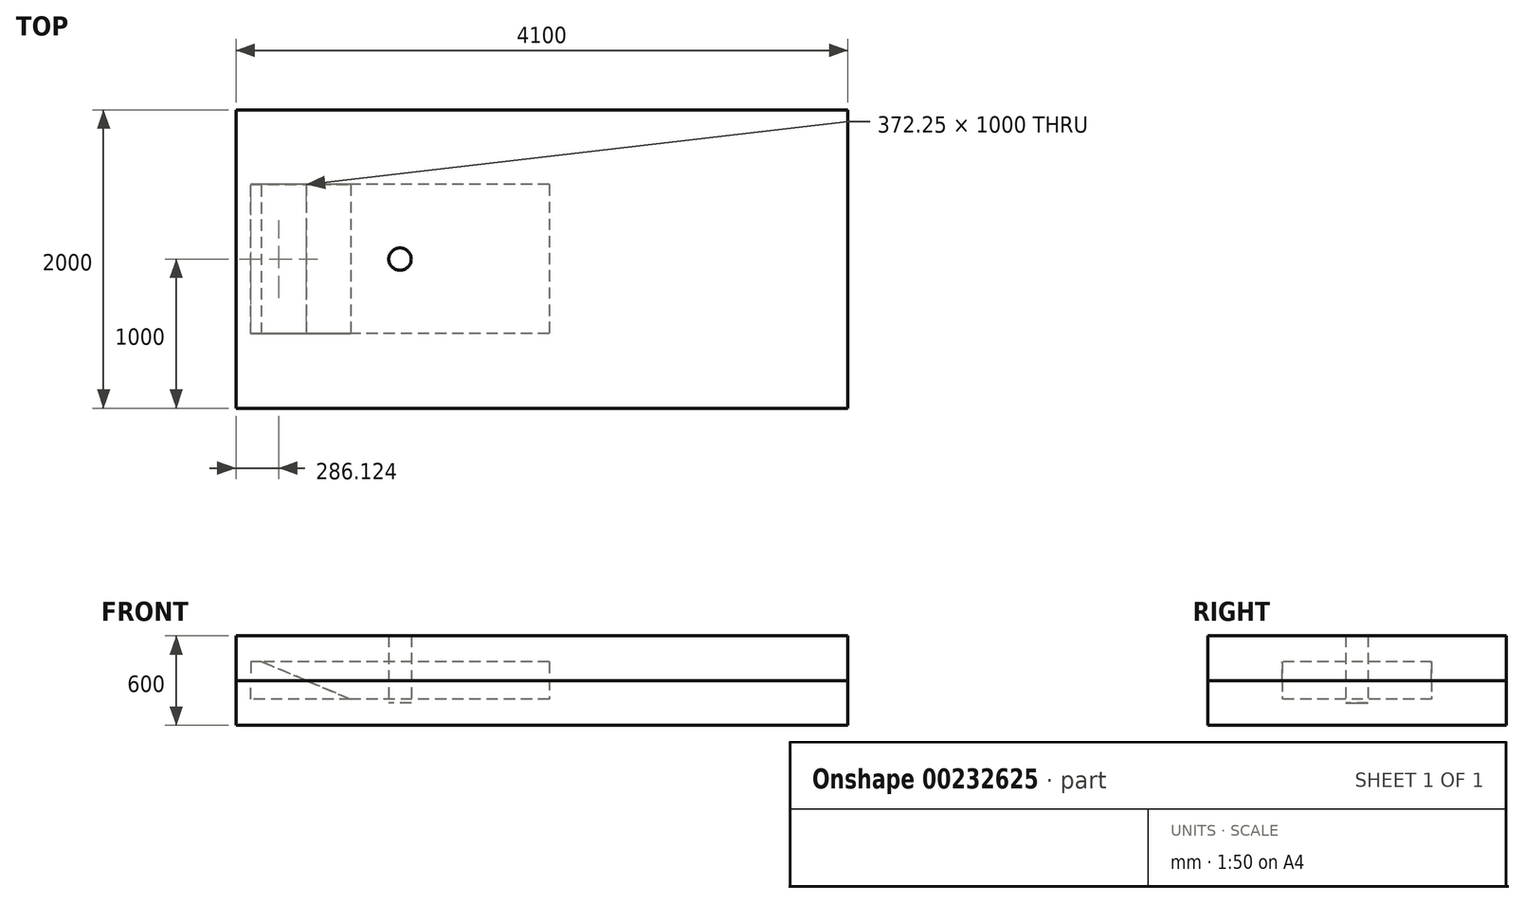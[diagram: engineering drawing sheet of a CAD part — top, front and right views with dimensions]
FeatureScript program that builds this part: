
annotation { "Feature Type Name" : "Feature", "Feature Type Description" : "" }
export const myFeature = defineFeature(function(context is Context, id is Id, definition is map)
    precondition{}
    {
        {
            var Q0;
            Q0=qCreatedBy(makeId("Top.planeOp"),FACE);
            var sketch = newSketch(context, id + "F0", { "sketchPlane" : qUnion([Q0])});
            skLineSegment(sketch, "E0.bottom", {"start": v(1000, 500) * mm, "end": v(-1000, 500) * mm});
            skLineSegment(sketch, "E0.top", {"start": v(1000, -500) * mm, "end": v(-1000, -500) * mm});
            skLineSegment(sketch, "E0.left", {"start": v(1000, 500) * mm, "end": v(1000, -500) * mm});
            skLineSegment(sketch, "E0.right", {"start": v(-1000, 500) * mm, "end": v(-1000, -500) * mm});
            skPoint(sketch, "E0.middle", {"position": v(0, 0) * mm});
            skSolve(sketch);
        }
        {
            var Q0;
            Q0=makeQuery(id+"F0.imprint","IMPRINT",FACE,{"disambiguationData":[TD([[makeQuery(id+"F0.imprint","IMPRINT",EDGE,{"derivedFrom":sQuery(id+"F0.wireOp",EDGE,"E0.bottom")}),1.0]])]});
            extrude(context, id + "F1", {"entities" : qUnion([Q0]), "endBound" : BoundingType.SYMMETRIC, "depth" : 250 * mm});
        }
        {
            var Q0;
            Q0=qCreatedBy(makeId("Top.planeOp"),FACE);
            var sketch = newSketch(context, id + "F2", { "sketchPlane" : qUnion([Q0])});
            skLineSegment(sketch, "E1.bottom", {"start": v(-1100, -1000) * mm, "end": v(3000, -1000) * mm});
            skLineSegment(sketch, "E1.top", {"start": v(-1100, 1000) * mm, "end": v(3000, 1000) * mm});
            skLineSegment(sketch, "E1.left", {"start": v(-1100, -1000) * mm, "end": v(-1100, 1000) * mm});
            skLineSegment(sketch, "E1.right", {"start": v(3000, -1000) * mm, "end": v(3000, 1000) * mm});
            skSolve(sketch);
        }
        {
            var Q0;
            Q0=makeQuery(id+"F2.imprint","IMPRINT",FACE,{"disambiguationData":[TD([[makeQuery(id+"F2.imprint","IMPRINT",EDGE,{"derivedFrom":sQuery(id+"F2.wireOp",EDGE,"E1.bottom")}),1.0]])]});
            extrude(context, id + "F3", {"entities" : qUnion([Q0]), "depth" : 300 * mm});
        }
        {
            var Q0;
            Q0 = qSketchRegion(id + "F2", true);
            extrude(context, id + "F4", {"entities" : qUnion([Q0]), "oppositeDirection" : true, "depth" : 300 * mm});
        }
        {
            var Q0;
            Q0=makeQuery(id+"F1.opExtrude","SWEPT_FACE",FACE,{"disambiguationData":[OSD([sQuery(id+"F0.wireOp",EDGE,"E0.top")])]});
            var sketch = newSketch(context, id + "F5", { "sketchPlane" : qUnion([Q0])});
            skLineSegment(sketch, "E2", {"start": v(-1000, 156.2) * mm, "end": v(-329.86, -125) * mm});
            skLineSegment(sketch, "E3", {"start": v(-329.86, -125) * mm, "end": v(-1000, -125) * mm});
            skLineSegment(sketch, "E4", {"start": v(-1000, -125) * mm, "end": v(-1000, 156.2) * mm});
            skSolve(sketch);
        }
        {
            var Q0;
            Q0 = qSketchRegion(id + "F5", true);
            extrude(context, id + "F6", {"entities" : qUnion([Q0]), "operationType" : NewBodyOperationType.REMOVE, "endBound" : BoundingType.UP_TO_NEXT, "oppositeDirection" : true, "depth" : 25 * mm});
        }
        {
            var Q0;
            Q0=qCreatedBy(makeId("Top.planeOp"),FACE);
            var sketch = newSketch(context, id + "F7", { "sketchPlane" : qUnion([Q0])});
            skCircle(sketch, "E5", {"center": v(0, 0) * mm, "radius": 75 * mm});
            skSolve(sketch);
        }
        {
            var Q0;
            Q0=makeQuery(id+"F7.imprint","IMPRINT",FACE,{"disambiguationData":[TD([[makeQuery(id+"F7.imprint","IMPRINT",EDGE,{"derivedFrom":sQuery(id+"F7.wireOp",EDGE,"E5")}),1.0]])]});
            extrude(context, id + "F8", {"entities" : qUnion([Q0]), "depth" : 300 * mm, "hasSecondDirection" : true, "secondDirectionOppositeDirection" : true, "secondDirectionDepth" : 150 * mm});
        }
    });
